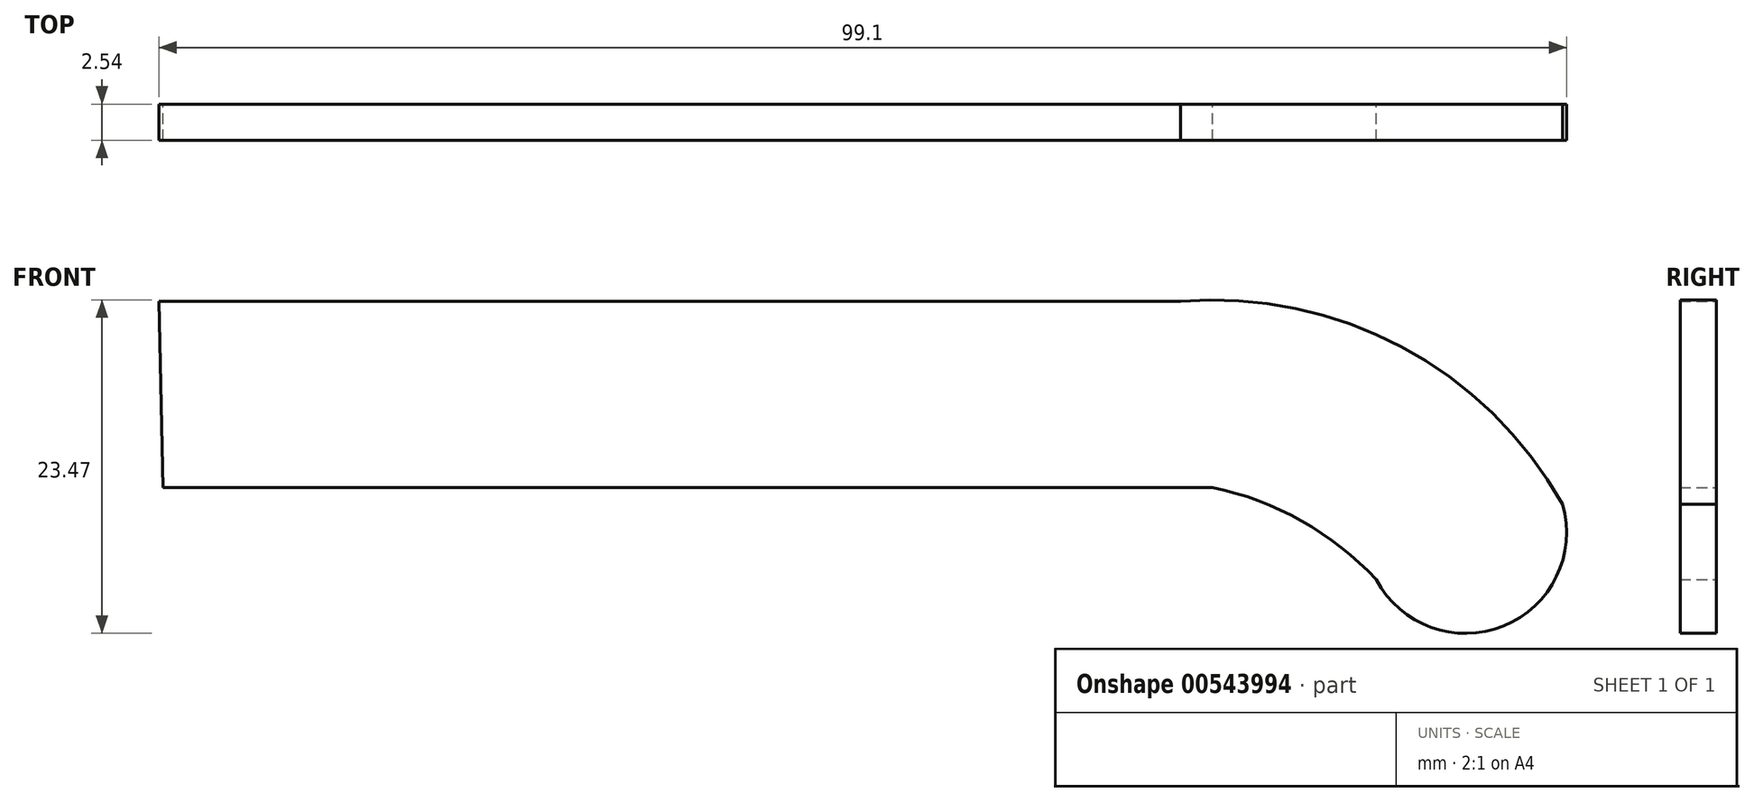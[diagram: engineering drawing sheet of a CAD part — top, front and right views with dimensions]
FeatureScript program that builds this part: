
annotation { "Feature Type Name" : "Feature", "Feature Type Description" : "" }
export const myFeature = defineFeature(function(context is Context, id is Id, definition is map)
    precondition{}
    {
        {
            var Q0;
            Q0=qCreatedBy(makeId("Front.planeOp"),FACE);
            var sketch = newSketch(context, id + "F0", { "sketchPlane" : qUnion([Q0])});
            skLineSegment(sketch, "E0", {"start": v(-51.15, 18.41) * mm, "end": v(20.8, 18.41) * mm});
            skLineSegment(sketch, "E1", {"start": v(-50.84, 5.31) * mm, "end": v(23.02, 5.31) * mm});
            skArc(sketch, "E2", {"start": v(34.56, -1.18) * mm, "mid": v(29.29, 2.96) * mm, "end": v(23.02, 5.31) * mm});
            skArc(sketch, "E3", {"start": v(47.67, 4.12) * mm, "mid": v(36.33, 15.21) * mm, "end": v(20.8, 18.41) * mm});
            skPoint(sketch, "E4", {"position": v(47.67, 4.12) * mm});
            skArc(sketch, "E5", {"start": v(34.56, -1.18) * mm, "mid": v(43.5, -4.45) * mm, "end": v(47.67, 4.12) * mm});
            skLineSegment(sketch, "E6", {"start": v(-51.15, 18.41) * mm, "end": v(-50.84, 5.31) * mm});
            skSolve(sketch);
        }
        {
            var Q0;
            Q0=makeQuery(id+"F0.imprint","IMPRINT",FACE,{"disambiguationData":[TD([[makeQuery(id+"F0.imprint","IMPRINT",EDGE,{"derivedFrom":sQuery(id+"F0.wireOp",EDGE,"E0")}),-1.0]])]});
            extrude(context, id + "F1", {"entities" : qUnion([Q0]), "depth" : 2.54 * mm, "offsetDistance" : 25.4 * mm});
        }
    });
